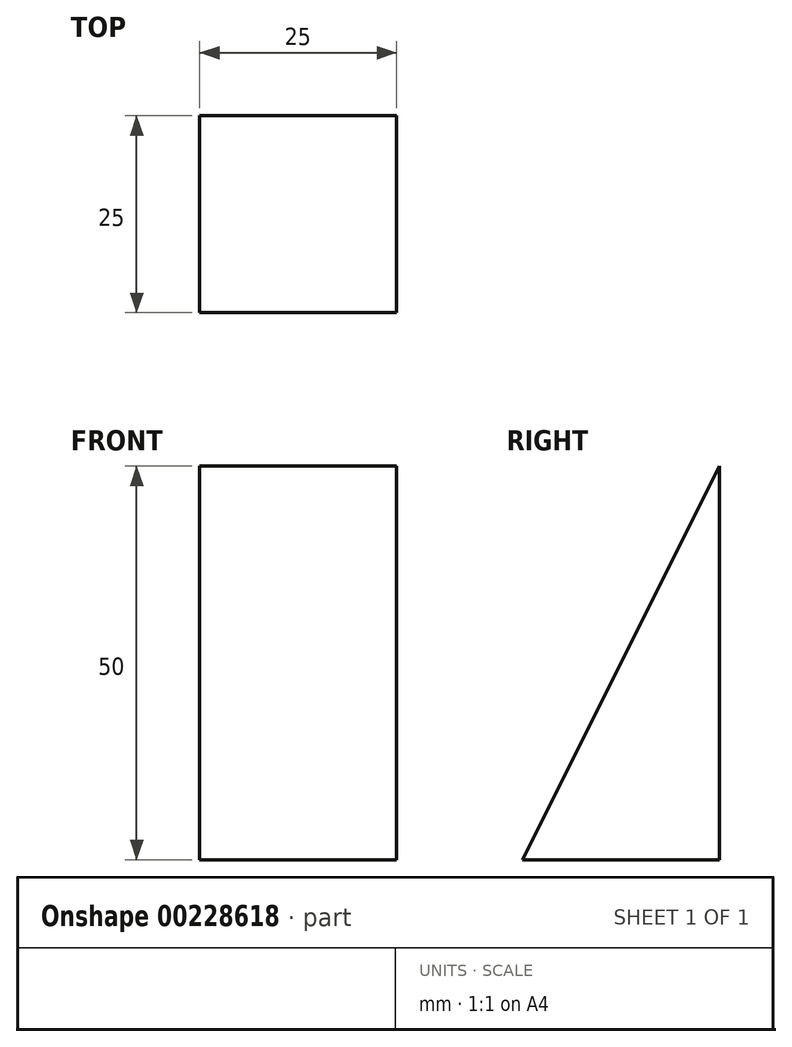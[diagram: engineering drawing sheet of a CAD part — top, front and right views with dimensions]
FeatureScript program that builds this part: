
annotation { "Feature Type Name" : "Feature", "Feature Type Description" : "" }
export const myFeature = defineFeature(function(context is Context, id is Id, definition is map)
    precondition{}
    {
        {
            var Q0;
            Q0=qCreatedBy(makeId("Top.planeOp"),FACE);
            var sketch = newSketch(context, id + "F0", { "sketchPlane" : qUnion([Q0])});
            skLineSegment(sketch, "E0.bottom", {"start": v(-12.5, 0) * mm, "end": v(12.5, 0) * mm});
            skLineSegment(sketch, "E0.top", {"start": v(-12.5, -25) * mm, "end": v(12.5, -25) * mm});
            skLineSegment(sketch, "E0.left", {"start": v(-12.5, 0) * mm, "end": v(-12.5, -25) * mm});
            skLineSegment(sketch, "E0.right", {"start": v(12.5, 0) * mm, "end": v(12.5, -25) * mm});
            skSolve(sketch);
        }
        {
            var Q0;
            Q0=makeQuery(id+"F0.imprint","IMPRINT",FACE,{"disambiguationData":[TD([[makeQuery(id+"F0.imprint","IMPRINT",EDGE,{"derivedFrom":sQuery(id+"F0.wireOp",EDGE,"E0.bottom")}),-1.0]])]});
            extrude(context, id + "F1", {"entities" : qUnion([Q0]), "depth" : 50 * mm, "offsetDistance" : 25 * mm});
        }
        {
            var Q0;
            Q0=makeQuery(id+"F1.opExtrude","SWEPT_FACE",FACE,{"disambiguationData":[OSD([sQuery(id+"F0.wireOp",EDGE,"E0.left")])]});
            var sketch = newSketch(context, id + "F2", { "sketchPlane" : qUnion([Q0])});
            skLineSegment(sketch, "E1", {"start": v(0, 50) * mm, "end": v(25, 0) * mm});
            skSolve(sketch);
        }
        {
            var Q0;
            Q0=makeQuery(id+"F2.imprint","IMPRINT",FACE,{"disambiguationData":[TD([[makeQuery(id+"F2.imprint","IMPRINT",EDGE,{"derivedFrom":sQuery(id+"F2.wireOp",EDGE,"E1")}),1.0]])]});
            extrude(context, id + "F3", {"entities" : qUnion([Q0]), "operationType" : NewBodyOperationType.REMOVE, "oppositeDirection" : true, "depth" : 25 * mm, "offsetDistance" : 25 * mm});
        }
    });
